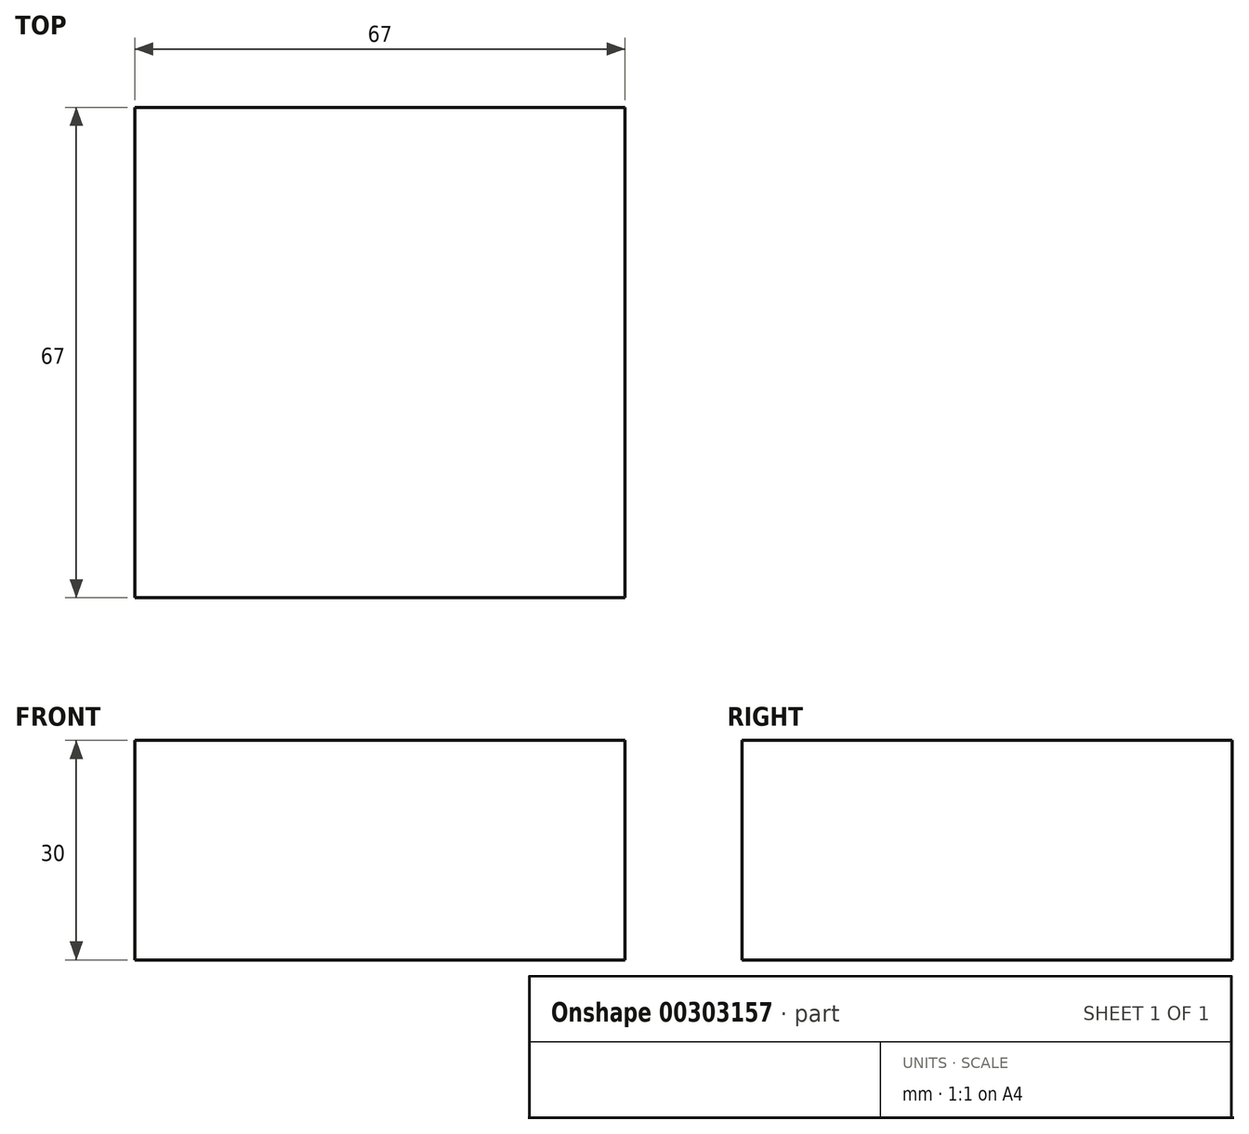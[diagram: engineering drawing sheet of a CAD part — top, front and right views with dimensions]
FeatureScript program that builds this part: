
annotation { "Feature Type Name" : "Feature", "Feature Type Description" : "" }
export const myFeature = defineFeature(function(context is Context, id is Id, definition is map)
    precondition{}
    {
        {
            var Q0;
            Q0=qCreatedBy(makeId("Top.planeOp"),FACE);
            var sketch = newSketch(context, id + "F0", { "sketchPlane" : qUnion([Q0])});
            skLineSegment(sketch, "E0.bottom", {"start": v(33.5, -33.5) * mm, "end": v(-33.5, -33.5) * mm});
            skLineSegment(sketch, "E0.top", {"start": v(33.5, 33.5) * mm, "end": v(-33.5, 33.5) * mm});
            skLineSegment(sketch, "E0.left", {"start": v(33.5, -33.5) * mm, "end": v(33.5, 33.5) * mm});
            skLineSegment(sketch, "E0.right", {"start": v(-33.5, -33.5) * mm, "end": v(-33.5, 33.5) * mm});
            skPoint(sketch, "E0.middle", {"position": v(0, 0) * mm});
            skSolve(sketch);
        }
        {
            var Q0;
            Q0=makeQuery(id+"F0.imprint","IMPRINT",FACE,{"disambiguationData":[TD([[makeQuery(id+"F0.imprint","IMPRINT",EDGE,{"derivedFrom":sQuery(id+"F0.wireOp",EDGE,"E0.bottom")}),-1.0]])]});
            extrude(context, id + "F1", {"entities" : qUnion([Q0]), "oppositeDirection" : true, "depth" : 30 * mm});
        }
    });
